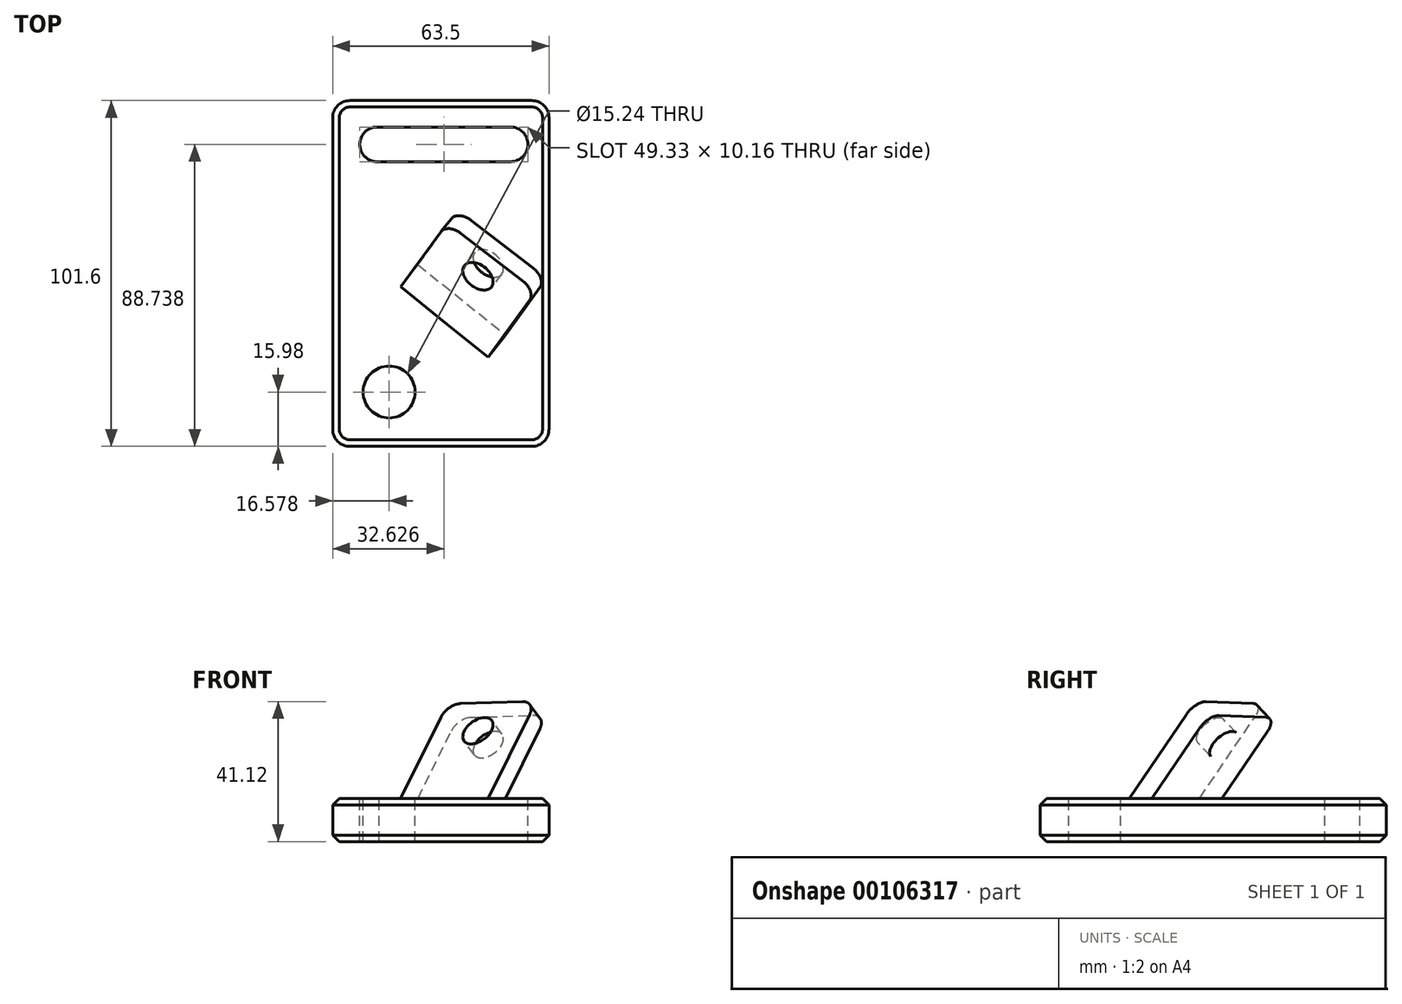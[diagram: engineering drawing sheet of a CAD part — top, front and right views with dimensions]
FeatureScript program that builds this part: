
annotation { "Feature Type Name" : "Feature", "Feature Type Description" : "" }
export const myFeature = defineFeature(function(context is Context, id is Id, definition is map)
    precondition{}
    {
        {
            var Q0;
            Q0=qCreatedBy(makeId("Top.planeOp"),FACE);
            var sketch = newSketch(context, id + "F0", { "sketchPlane" : qUnion([Q0])});
            skLineSegment(sketch, "E0.bottom", {"start": v(-31.75, 50.8) * mm, "end": v(31.75, 50.8) * mm});
            skLineSegment(sketch, "E0.top", {"start": v(-31.75, -50.8) * mm, "end": v(31.75, -50.8) * mm});
            skLineSegment(sketch, "E0.left", {"start": v(-31.75, 50.8) * mm, "end": v(-31.75, -50.8) * mm});
            skLineSegment(sketch, "E0.right", {"start": v(31.75, 50.8) * mm, "end": v(31.75, -50.8) * mm});
            skSolve(sketch);
        }
        {
            var Q0;
            Q0=makeQuery(id+"F0.imprint","IMPRINT",FACE,{"disambiguationData":[TD([[makeQuery(id+"F0.imprint","IMPRINT",EDGE,{"derivedFrom":sQuery(id+"F0.wireOp",EDGE,"E0.bottom")}),-1.0]])]});
            extrude(context, id + "F1", {"entities" : qUnion([Q0]), "depth" : 12.7 * mm});
        }
        {
            var Q0;
            Q0=makeQuery(id+"F1.opExtrude","CAP_FACE",FACE,{"disambiguationData":[OSD([sQuery(id+"F0.wireOp",EDGE,"E0.bottom"),sQuery(id+"F0.wireOp",EDGE,"E0.top"),sQuery(id+"F0.wireOp",EDGE,"E0.left"),sQuery(id+"F0.wireOp",EDGE,"E0.right")])],"isStart":false});
            var sketch = newSketch(context, id + "F2", { "sketchPlane" : qUnion([Q0])});
            skLineSegment(sketch, "E1", {"start": v(-31.75, 12.04) * mm, "end": v(31.75, -38.93) * mm});
            skSolve(sketch);
        }
        {
            var Q0;
            Q0=sQuery(id+"F2.wireOp",EDGE,"E1");
            cPlane(context, id + "F3", {"entities" : qUnion([Q0]), "cplaneType" : CPlaneType.LINE_ANGLE, "offset" : 25.4 * mm, "angle" : 140 * degree, "width" : 152.4 * mm, "height" : 152.4 * mm});
        }
        {
            var Q0;
            Q0=qCreatedBy(id+"F3.planeOp",FACE);
            var sketch = newSketch(context, id + "F4", { "sketchPlane" : qUnion([Q0])});
            skLineSegment(sketch, "E2", {"start": v(-4.5, 5.87) * mm, "end": v(11.03, 38.43) * mm});
            skLineSegment(sketch, "E3", {"start": v(11.03, 38.43) * mm, "end": v(40.75, 24.26) * mm});
            skLineSegment(sketch, "E4", {"start": v(40.75, 24.26) * mm, "end": v(24.65, -9.53) * mm});
            skLineSegment(sketch, "E5", {"start": v(24.65, -9.53) * mm, "end": v(-4.5, 5.87) * mm});
            skSolve(sketch);
        }
        {
            var Q0;
            Q0=makeQuery(id+"F4.imprint","IMPRINT",FACE,{"disambiguationData":[TD([[makeQuery(id+"F4.imprint","IMPRINT",EDGE,{"derivedFrom":sQuery(id+"F4.wireOp",EDGE,"E2")}),-1.0]])]});
            extrude(context, id + "F5", {"entities" : qUnion([Q0]), "operationType" : NewBodyOperationType.ADD, "oppositeDirection" : true, "depth" : 6.35 * mm});
        }
        {
            var Q0;
            Q0=makeQuery(id+"F5.opExtrude","SWEPT_EDGE",EDGE,{"disambiguationData":[OSD([sQuery(id+"F4.wireOp",EDGE,"E2"),sQuery(id+"F4.wireOp",EDGE,"E3")])]});
            var Q1;
            Q1=makeQuery(id+"F5.opExtrude","SWEPT_EDGE",EDGE,{"disambiguationData":[OSD([sQuery(id+"F4.wireOp",EDGE,"E3"),sQuery(id+"F4.wireOp",EDGE,"E4")])]});
            fillet(context, id + "F6", {"entities" : qUnion([Q0, Q1]), "radius" : 5.08 * mm, "tangentPropagation" : true, "allowEdgeOverflow" : false});
        }
        {
            var Q0;
            Q0=makeQuery(id+"F5.opExtrude","CAP_FACE",FACE,{"disambiguationData":[OSD([sQuery(id+"F4.wireOp",EDGE,"E2"),sQuery(id+"F4.wireOp",EDGE,"E3"),sQuery(id+"F4.wireOp",EDGE,"E4"),sQuery(id+"F4.wireOp",EDGE,"E5")])],"isStart":true});
            var sketch = newSketch(context, id + "F7", { "sketchPlane" : qUnion([Q0])});
            skPoint(sketch, "E6", {"position": v(21.25, 21.59) * mm});
            skSolve(sketch);
        }
        {
            var Q0;
            Q0=sQuery(id+"F7.wireOp",VERTEX,"E6");
            var Q1;
            Q1=makeQuery(id+"F1.opExtrude","SWEPT_BODY",BODY,{"disambiguationData":[OSD([sQuery(id+"F0.wireOp",EDGE,"E0.bottom"),sQuery(id+"F0.wireOp",EDGE,"E0.top"),sQuery(id+"F0.wireOp",EDGE,"E0.left"),sQuery(id+"F0.wireOp",EDGE,"E0.right")])]});
            hole(context, id + "F8", {"style" : HoleStyle.SIMPLE, "endStyle" : HoleEndStyle.BLIND, "holeDiameter" : 10.16 * mm, "holeDepth" : 6.35 * mm, "startFromSketch" : true, "locations" : qUnion([Q0]), "scope" : qUnion([Q1])});
        }
        {
            var Q0;
            {var subQ0=sQuery(id+"F2.wireOp",EDGE,"E1");Q0=makeQuery(id+"F2.imprint","IMPRINT",FACE,{"disambiguationData":[TD([[makeQuery(id+"F2.imprint","IMPRINT",EDGE,{"derivedFrom":subQ0}),-1.0]])]});}
            var sketch = newSketch(context, id + "F9", { "sketchPlane" : qUnion([Q0])});
            skPoint(sketch, "E7", {"position": v(-15.17, -34.82) * mm});
            skSolve(sketch);
        }
        {
            var Q0;
            Q0=sQuery(id+"F9.wireOp",VERTEX,"E7");
            var Q1;
            Q1=makeQuery(id+"F1.opExtrude","SWEPT_BODY",BODY,{"disambiguationData":[OSD([sQuery(id+"F0.wireOp",EDGE,"E0.bottom"),sQuery(id+"F0.wireOp",EDGE,"E0.top"),sQuery(id+"F0.wireOp",EDGE,"E0.left"),sQuery(id+"F0.wireOp",EDGE,"E0.right")])]});
            hole(context, id + "F10", {"style" : HoleStyle.SIMPLE, "endStyle" : HoleEndStyle.BLIND, "holeDiameter" : 15.24 * mm, "holeDepth" : 12.7 * mm, "startFromSketch" : true, "locations" : qUnion([Q0]), "scope" : qUnion([Q1])});
        }
        {
            var Q0;
            {var subQ0=sQuery(id+"F2.wireOp",EDGE,"E1");Q0=makeQuery(id+"F2.imprint","IMPRINT",FACE,{"disambiguationData":[TD([[makeQuery(id+"F2.imprint","IMPRINT",EDGE,{"derivedFrom":subQ0}),1.0]])]});}
            var sketch = newSketch(context, id + "F11", { "sketchPlane" : qUnion([Q0])});
            skLineSegment(sketch, "E8", {"start": v(-18.15, 32.86) * mm, "end": v(20.46, 32.86) * mm});
            skArc(sketch, "E9", {"start": v(20.46, 32.86) * mm, "mid": v(25.54, 37.94) * mm, "end": v(20.46, 43.02) * mm});
            skLineSegment(sketch, "E10", {"start": v(20.46, 43.02) * mm, "end": v(-18.7, 43.02) * mm});
            skArc(sketch, "E11", {"start": v(-18.7, 43.02) * mm, "mid": v(-23.79, 37.65) * mm, "end": v(-18.15, 32.86) * mm});
            skSolve(sketch);
        }
        {
            var Q0;
            Q0 = qSketchRegion(id + "F11", true);
            extrude(context, id + "F12", {"entities" : qUnion([Q0]), "operationType" : NewBodyOperationType.REMOVE, "oppositeDirection" : true, "depth" : 25.4 * mm});
        }
        {
            var Q0;
            Q0=makeQuery(id+"F1.opExtrude","SWEPT_EDGE",EDGE,{"disambiguationData":[OSD([sQuery(id+"F0.wireOp",EDGE,"E0.bottom"),sQuery(id+"F0.wireOp",EDGE,"E0.left")])]});
            var Q1;
            Q1=makeQuery(id+"F1.opExtrude","SWEPT_EDGE",EDGE,{"disambiguationData":[OSD([sQuery(id+"F0.wireOp",EDGE,"E0.top"),sQuery(id+"F0.wireOp",EDGE,"E0.left")])]});
            var Q2;
            Q2=makeQuery(id+"F1.opExtrude","SWEPT_EDGE",EDGE,{"disambiguationData":[OSD([sQuery(id+"F0.wireOp",EDGE,"E0.top"),sQuery(id+"F0.wireOp",EDGE,"E0.right")])]});
            var Q3;
            Q3=makeQuery(id+"F1.opExtrude","SWEPT_EDGE",EDGE,{"disambiguationData":[OSD([sQuery(id+"F0.wireOp",EDGE,"E0.bottom"),sQuery(id+"F0.wireOp",EDGE,"E0.right")])]});
            fillet(context, id + "F13", {"entities" : qUnion([Q0, Q1, Q2, Q3]), "radius" : 5.08 * mm, "tangentPropagation" : true, "allowEdgeOverflow" : false});
        }
        {
            var Q0;
            Q0=makeQuery(id+"F1.opExtrude","CAP_EDGE",EDGE,{"disambiguationData":[OSD([sQuery(id+"F0.wireOp",EDGE,"E0.left")])],"isStart":false});
            var Q1;
            Q1=makeQuery(id+"F1.opExtrude","CAP_EDGE",EDGE,{"disambiguationData":[OSD([sQuery(id+"F0.wireOp",EDGE,"E0.bottom")])],"isStart":false});
            var Q2;
            {var subQ0=sQuery(id+"F0.wireOp",EDGE,"E0.left");var subQ1=sQuery(id+"F0.wireOp",EDGE,"E0.bottom");Q2=makeQuery(id+"F13.opFillet","BLEND_EDGE",EDGE,{"blendedFrom":[makeQuery(id+"F1.opExtrude","SWEPT_EDGE",EDGE,{"disambiguationData":[OSD([subQ1,subQ0])]}),makeQuery(id+"F1.opExtrude","CAP_FACE",FACE,{"disambiguationData":[OSD([subQ1,sQuery(id+"F0.wireOp",EDGE,"E0.top"),subQ0,sQuery(id+"F0.wireOp",EDGE,"E0.right")])],"isStart":false})],"blendedInto":[makeQuery(id+"F1.opExtrude","CAP_FACE",FACE,{"disambiguationData":[OSD([subQ1,sQuery(id+"F0.wireOp",EDGE,"E0.top"),subQ0,sQuery(id+"F0.wireOp",EDGE,"E0.right")])],"isStart":false})]});}
            var Q3;
            {var subQ0=sQuery(id+"F0.wireOp",EDGE,"E0.right");var subQ1=sQuery(id+"F0.wireOp",EDGE,"E0.bottom");Q3=makeQuery(id+"F13.opFillet","BLEND_EDGE",EDGE,{"blendedFrom":[makeQuery(id+"F1.opExtrude","SWEPT_EDGE",EDGE,{"disambiguationData":[OSD([subQ1,subQ0])]}),makeQuery(id+"F1.opExtrude","CAP_FACE",FACE,{"disambiguationData":[OSD([subQ1,sQuery(id+"F0.wireOp",EDGE,"E0.top"),sQuery(id+"F0.wireOp",EDGE,"E0.left"),subQ0])],"isStart":false})],"blendedInto":[makeQuery(id+"F1.opExtrude","CAP_FACE",FACE,{"disambiguationData":[OSD([subQ1,sQuery(id+"F0.wireOp",EDGE,"E0.top"),sQuery(id+"F0.wireOp",EDGE,"E0.left"),subQ0])],"isStart":false})]});}
            var Q4;
            Q4=makeQuery(id+"F1.opExtrude","CAP_EDGE",EDGE,{"disambiguationData":[OSD([sQuery(id+"F0.wireOp",EDGE,"E0.right")])],"isStart":false});
            var Q5;
            {var subQ0=sQuery(id+"F0.wireOp",EDGE,"E0.right");var subQ1=sQuery(id+"F0.wireOp",EDGE,"E0.top");Q5=makeQuery(id+"F13.opFillet","BLEND_EDGE",EDGE,{"blendedFrom":[makeQuery(id+"F1.opExtrude","SWEPT_EDGE",EDGE,{"disambiguationData":[OSD([subQ1,subQ0])]}),makeQuery(id+"F1.opExtrude","CAP_FACE",FACE,{"disambiguationData":[OSD([sQuery(id+"F0.wireOp",EDGE,"E0.bottom"),subQ1,sQuery(id+"F0.wireOp",EDGE,"E0.left"),subQ0])],"isStart":false})],"blendedInto":[makeQuery(id+"F1.opExtrude","CAP_FACE",FACE,{"disambiguationData":[OSD([sQuery(id+"F0.wireOp",EDGE,"E0.bottom"),subQ1,sQuery(id+"F0.wireOp",EDGE,"E0.left"),subQ0])],"isStart":false})]});}
            var Q6;
            Q6=makeQuery(id+"F1.opExtrude","CAP_EDGE",EDGE,{"disambiguationData":[OSD([sQuery(id+"F0.wireOp",EDGE,"E0.top")])],"isStart":false});
            var Q7;
            {var subQ0=sQuery(id+"F0.wireOp",EDGE,"E0.left");var subQ1=sQuery(id+"F0.wireOp",EDGE,"E0.top");Q7=makeQuery(id+"F13.opFillet","BLEND_EDGE",EDGE,{"blendedFrom":[makeQuery(id+"F1.opExtrude","SWEPT_EDGE",EDGE,{"disambiguationData":[OSD([subQ1,subQ0])]}),makeQuery(id+"F1.opExtrude","CAP_FACE",FACE,{"disambiguationData":[OSD([sQuery(id+"F0.wireOp",EDGE,"E0.bottom"),subQ1,subQ0,sQuery(id+"F0.wireOp",EDGE,"E0.right")])],"isStart":false})],"blendedInto":[makeQuery(id+"F1.opExtrude","CAP_FACE",FACE,{"disambiguationData":[OSD([sQuery(id+"F0.wireOp",EDGE,"E0.bottom"),subQ1,subQ0,sQuery(id+"F0.wireOp",EDGE,"E0.right")])],"isStart":false})]});}
            chamfer(context, id + "F14", {"entities" : qUnion([Q0, Q1, Q2, Q3, Q4, Q5, Q6, Q7]), "width" : 1.9 * mm, "tangentPropagation" : true});
        }
        {
            var Q0;
            Q0=makeQuery(id+"F1.opExtrude","CAP_EDGE",EDGE,{"disambiguationData":[OSD([sQuery(id+"F0.wireOp",EDGE,"E0.left")])],"isStart":true});
            var Q1;
            {var subQ0=sQuery(id+"F0.wireOp",EDGE,"E0.left");var subQ1=sQuery(id+"F0.wireOp",EDGE,"E0.bottom");Q1=makeQuery(id+"F13.opFillet","BLEND_EDGE",EDGE,{"blendedFrom":[makeQuery(id+"F1.opExtrude","SWEPT_EDGE",EDGE,{"disambiguationData":[OSD([subQ1,subQ0])]}),makeQuery(id+"F1.opExtrude","CAP_FACE",FACE,{"disambiguationData":[OSD([subQ1,sQuery(id+"F0.wireOp",EDGE,"E0.top"),subQ0,sQuery(id+"F0.wireOp",EDGE,"E0.right")])],"isStart":true})],"blendedInto":[makeQuery(id+"F1.opExtrude","CAP_FACE",FACE,{"disambiguationData":[OSD([subQ1,sQuery(id+"F0.wireOp",EDGE,"E0.top"),subQ0,sQuery(id+"F0.wireOp",EDGE,"E0.right")])],"isStart":true})]});}
            var Q2;
            Q2=makeQuery(id+"F1.opExtrude","CAP_EDGE",EDGE,{"disambiguationData":[OSD([sQuery(id+"F0.wireOp",EDGE,"E0.bottom")])],"isStart":true});
            var Q3;
            {var subQ0=sQuery(id+"F0.wireOp",EDGE,"E0.right");var subQ1=sQuery(id+"F0.wireOp",EDGE,"E0.bottom");Q3=makeQuery(id+"F13.opFillet","BLEND_EDGE",EDGE,{"blendedFrom":[makeQuery(id+"F1.opExtrude","SWEPT_EDGE",EDGE,{"disambiguationData":[OSD([subQ1,subQ0])]}),makeQuery(id+"F1.opExtrude","CAP_FACE",FACE,{"disambiguationData":[OSD([subQ1,sQuery(id+"F0.wireOp",EDGE,"E0.top"),sQuery(id+"F0.wireOp",EDGE,"E0.left"),subQ0])],"isStart":true})],"blendedInto":[makeQuery(id+"F1.opExtrude","CAP_FACE",FACE,{"disambiguationData":[OSD([subQ1,sQuery(id+"F0.wireOp",EDGE,"E0.top"),sQuery(id+"F0.wireOp",EDGE,"E0.left"),subQ0])],"isStart":true})]});}
            var Q4;
            Q4=makeQuery(id+"F1.opExtrude","CAP_EDGE",EDGE,{"disambiguationData":[OSD([sQuery(id+"F0.wireOp",EDGE,"E0.right")])],"isStart":true});
            var Q5;
            {var subQ0=sQuery(id+"F0.wireOp",EDGE,"E0.right");var subQ1=sQuery(id+"F0.wireOp",EDGE,"E0.top");Q5=makeQuery(id+"F13.opFillet","BLEND_EDGE",EDGE,{"blendedFrom":[makeQuery(id+"F1.opExtrude","SWEPT_EDGE",EDGE,{"disambiguationData":[OSD([subQ1,subQ0])]}),makeQuery(id+"F1.opExtrude","CAP_FACE",FACE,{"disambiguationData":[OSD([sQuery(id+"F0.wireOp",EDGE,"E0.bottom"),subQ1,sQuery(id+"F0.wireOp",EDGE,"E0.left"),subQ0])],"isStart":true})],"blendedInto":[makeQuery(id+"F1.opExtrude","CAP_FACE",FACE,{"disambiguationData":[OSD([sQuery(id+"F0.wireOp",EDGE,"E0.bottom"),subQ1,sQuery(id+"F0.wireOp",EDGE,"E0.left"),subQ0])],"isStart":true})]});}
            var Q6;
            Q6=makeQuery(id+"F1.opExtrude","CAP_EDGE",EDGE,{"disambiguationData":[OSD([sQuery(id+"F0.wireOp",EDGE,"E0.top")])],"isStart":true});
            var Q7;
            {var subQ0=sQuery(id+"F0.wireOp",EDGE,"E0.left");var subQ1=sQuery(id+"F0.wireOp",EDGE,"E0.top");Q7=makeQuery(id+"F13.opFillet","BLEND_EDGE",EDGE,{"blendedFrom":[makeQuery(id+"F1.opExtrude","SWEPT_EDGE",EDGE,{"disambiguationData":[OSD([subQ1,subQ0])]}),makeQuery(id+"F1.opExtrude","CAP_FACE",FACE,{"disambiguationData":[OSD([sQuery(id+"F0.wireOp",EDGE,"E0.bottom"),subQ1,subQ0,sQuery(id+"F0.wireOp",EDGE,"E0.right")])],"isStart":true})],"blendedInto":[makeQuery(id+"F1.opExtrude","CAP_FACE",FACE,{"disambiguationData":[OSD([sQuery(id+"F0.wireOp",EDGE,"E0.bottom"),subQ1,subQ0,sQuery(id+"F0.wireOp",EDGE,"E0.right")])],"isStart":true})]});}
            chamfer(context, id + "F15", {"entities" : qUnion([Q0, Q1, Q2, Q3, Q4, Q5, Q6, Q7]), "width" : 1.9 * mm, "tangentPropagation" : true});
        }
    });
